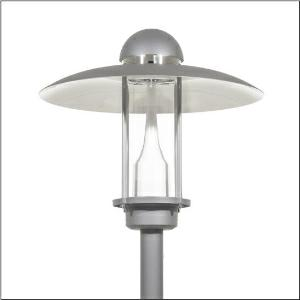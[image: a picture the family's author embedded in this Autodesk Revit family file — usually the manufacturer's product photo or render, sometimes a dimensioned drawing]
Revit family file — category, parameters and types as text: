
# Revit family: city-light_elegance_iq___p1_0a_5xa5265bf14h_371a
name_source: partatom
category: Lighting Fixtures
units: mm (PartAtom-declared; Revit-internal decimal feet)

## family parameters
Cut with Voids When Loaded = No
Host = Face
Light Source = No
Part Type = Normal
Room Calculation Point = No
Round Connector Dimension = Use Diameter
Shared = No

## types (1)
- --- (1 x LED, 1440 lm, 12.9 W, 2200K)
    Apparent Load = 13 VA
    CIE Flux Codes = 32 62 91 97 100
    Color Rendering = 70
    Color Temperature = 2200K
    Default Elevation = 1800 mm
    Description = City-Light Elegance iQ, mast luminaire, Module 540 iQ-SR, primary light control with 3 zone facetted reflector, of plastic, silver coated, highly specular, structured, primary optical cover: cover, of PMMA, transparent, light distribution: P1.0a, light emission: direct distribution, primary light characteristic: strongly asymmetric, installation type: post-top, LED, High Power LED, rated luminous flux: 1.440lm, luminous efficacy: 112lm/W, light colour: 722, colour temperature: 2200K, control gear: ECG iQ, control: presetting dimming logarithmic, Street-Remote, Auto-Match, Temp-Guard, Lumen-Switch, Night-Set, Smart-Wire, Light-Fading, Desk-Remote (wireless, voltage-free reading and setting of iQ features in the workshop via application-optimized NFC function/RFID function), optimised constant luminous flux control (CLO 2.0), with terminal, 6-pole, max. 2.5mm², mains connection: 230..240V, AC, 50/60Hz, start of lifetime: 13W, end of service life: 13W, reduction: 6W, luminaire housing, upper part, of aluminium, coated, Siteco® metallic grey (DB 702S), diameter: 750mm, height: 675mm, spigot size: d x l = 76 x 70mm (post-top) | with reducer (optional accessory) 60 x 70mm, post-top mast mounting element, of diecast aluminium, coated, Siteco® metallic grey (DB 702S), Module 540 iQ-SR, traffic white (RAL 9016), equipment: standard, protection rating (complete): IP65, insulation class (complete): insulation class II (safety insulation), certification: CE, ENEC, VDE, packaging unit: 1 piece

Light Distribution: P1.0a
    Height = 675 mm
    Lamp = 1 x LED
    Lamp Light Flux = 1440 lm
    Lamp Power = 12.9 W
    Lamp count = 1
    Length = 750 mm
    Luminous efficacy = 112 lm/W
    Manufacturer = Siteco
    ModVariant = No
    Model = 5XA5265BF14H
    Number of Poles = 1
    OnlyDefault = Yes
    Power Factor = 1
    Product Name = City-Light Elegance iQ | P1.0a
    Product group = mast luminaire | pylon top
    ProductGroupID = 6100
    Protection Class = Protection class II
    Protection Degree = IP 65
    RLX_Detail_Level = 1
    RLX_Emergency_Light_Flux = 0 lm
    RLX_Emergency_Type = 0
    RLX_Emergency_Type_DB = No
    RlxData = <blob elided: 102461 chars, md5=30bcfb03>
    Socket = socket
    Standby Power = 0 W
    System Light Flux = 1440 lm
    System Power = 13 W
    Type Comments = factory setting: luminous flux: 100 % | dim-lin: 254 | 516 mA
    Type Image = l_1006912.jpg
    URL = http://relux.com
    VarID = @adj_092081
    Voltage = 0 V
    Weight = 0.00 kg
    Width = 0 mm  [stored 0 ft]

note: [stored X ft] marks values corroborated as IEEE doubles in the binary element streams (Revit-internal decimal feet)

## geometry (parser evidence)
native form markers: Blend x4, Sweep x11
no freeform markers — native parametric forms only
